# Revit family: Low_Profile_Grease_Interceptor-Zurn-Z1171
name_source: partatom
category: Plumbing Fixtures
units: mm (PartAtom-declared; Revit-internal decimal feet)

## family parameters
Always vertical = Yes
Cut with Voids When Loaded = No
Maintain Annotation Orientation = No
OmniClass Number = 23.45.30.00
OmniClass Title = Washing and Waste Disposal Equipment
Part Type = Normal
Room Calculation Point = No
Round Connector Dimension = Use Radius
Shared = No
Work Plane-Based = No

## types (6) — shared parameters
Assembly Code = D2090300
CW Connection = No
CWFU = 1
Default Elevation = 20 "
Description = Low Profile Grease Interceptor
HW Connection = No
Inlet/Outlet Connetor Radius = 1.5 "
Inlet/Outlet Diameter (Actual) = 3.5 "
Inlet/Outlet Diameter (Nominal) = 3 "
Manufacturer = Zurn Water, LLC
Manufacurer Brand = Zurn
Modified Date = 07/24/25
Product Documentation Link = https://files.zurn.com
Product Installation Sheet URL = https://files.zurn.com
Product Page URL = https://www.zurn.com
Product data url = https://www.bimobject.com
URL = www.zurn.com
Vent Connection = No
Waste Connection = Yes
zero-valued in all types: HWFU, WFU

## per-type parameters (varying)
| type | Approx. Weight (Lbs) | Capacity Grease Lbs | Capacity Water Gal | Cutout | Dimension (H) | Height of Body (C) | Inlet/Outlet (D/E) | Main Material | Model | Overall Length (F) | Width of Body (G) |
| Z1171-500 (3 Inch 20 G.P.M) | 102 " | 40 " | 15 " | 10.375 " | 6.75 " | 10 " | 3.125 " | Steel - Zurn - Fabricated - Acid resistant Coated | Z1171 | 32.375 " | 20.75 " |
| Z1171-700 (3 Inch 35 G.P.M) | 172 " | 70 " | 30 " | 14.5 " | 7 " | 10.75 " | 3.313 " | Steel - Zurn - Fabricated - Acid resistant Coated | Z1171 | 43.5 " | 29 " |
| Z1171-800 (3 Inch 50 G.P.M) | 210 " | 100 " | 45 " | 14.5 " | 10 " | 16 " | 10 " | Steel - Zurn - Fabricated - Acid resistant Coated | Z1171 | 49.875 " | 29 " |
| ZS1171-500 (3 Inch 20 G.P.M) | 102 " | 40 " | 15 " | 10.375 " | 6.75 " | 10 " | 3.125 " | Steel - Zurn - Fabricated Stainless - Type 304 | ZS1171 | 32.375 " | 20.75 " |
| ZS1171-700 (3 Inch 35 G.P.M) | 172 " | 70 " | 30 " | 14.5 " | 7 " | 10.75 " | 3.313 " | Steel - Zurn - Fabricated Stainless - Type 304 | ZS1171 | 43.5 " | 29 " |
| ZS1171-800 (3 Inch 50 G.P.M) | 210 " | 100 " | 45 " | 14.5 " | 10 " | 16 " | 10 " | Steel - Zurn - Fabricated Stainless - Type 304 | ZS1171 | 49.875 " | 29 " |

## geometry (parser evidence)
native form markers: Sweep x2
no freeform markers — native parametric forms only
